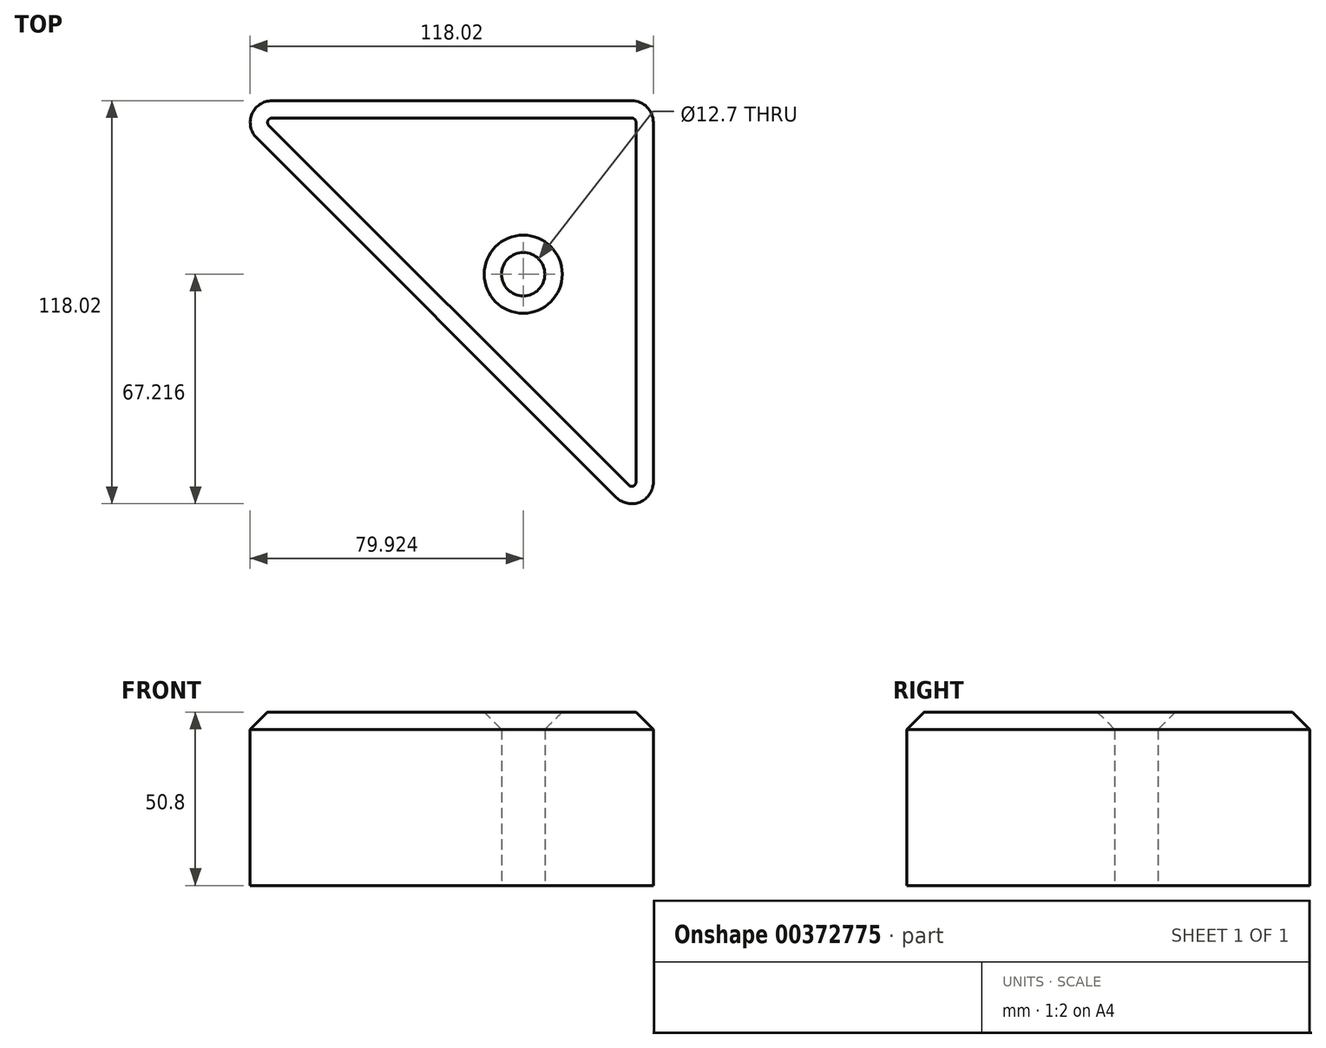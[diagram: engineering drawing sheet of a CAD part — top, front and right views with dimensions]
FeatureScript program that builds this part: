
annotation { "Feature Type Name" : "Feature", "Feature Type Description" : "" }
export const myFeature = defineFeature(function(context is Context, id is Id, definition is map)
    precondition{}
    {
        {
            var Q0;
            Q0=qCreatedBy(makeId("Top.planeOp"),FACE);
            var sketch = newSketch(context, id + "F0", { "sketchPlane" : qUnion([Q0])});
            skLineSegment(sketch, "E0", {"start": v(-67.08, 34.78) * mm, "end": v(38.24, 34.78) * mm});
            skLineSegment(sketch, "E1", {"start": v(44.6, 28.43) * mm, "end": v(44.6, -76.9) * mm});
            skLineSegment(sketch, "E2", {"start": v(33.75, -81.38) * mm, "end": v(-71.57, 23.94) * mm});
            skCircle(sketch, "E3", {"center": v(6.5, -16.02) * mm, "radius": 6.35 * mm});
            skPoint(sketch, "E4.visualSharp", {"position": v(-82.4, 34.78) * mm});
            skArc(sketch, "E4.filletArc", {"start": v(-67.08, 34.78) * mm, "mid": v(-72.94, 30.86) * mm, "end": v(-71.57, 23.94) * mm});
            skPoint(sketch, "E5.visualSharp", {"position": v(44.6, 34.78) * mm});
            skArc(sketch, "E5.filletArc", {"start": v(44.6, 28.43) * mm, "mid": v(42.73, 32.92) * mm, "end": v(38.24, 34.78) * mm});
            skPoint(sketch, "E6.visualSharp", {"position": v(44.6, -92.22) * mm});
            skArc(sketch, "E6.filletArc", {"start": v(33.75, -81.38) * mm, "mid": v(40.67, -82.76) * mm, "end": v(44.6, -76.9) * mm});
            skLineSegment(sketch, "E7", {"start": v(0, 0) * mm, "end": v(6.5, -16.02) * mm, "construction": true});
            skLineSegment(sketch, "E8", {"start": v(6.5, -16.02) * mm, "end": v(0, -16.02) * mm});
            skLineSegment(sketch, "E9", {"start": v(0, -16.02) * mm, "end": v(0, 0) * mm, "construction": true});
            skSolve(sketch);
        }
        {
            var Q0;
            Q0=makeQuery(id+"F0.imprint","IMPRINT",FACE,{"disambiguationData":[TD([[makeQuery(id+"F0.imprint","IMPRINT",EDGE,{"derivedFrom":sQuery(id+"F0.wireOp",EDGE,"E0")}),-1.0]])]});
            extrude(context, id + "F1", {"entities" : qUnion([Q0]), "depth" : 50.8 * mm});
        }
        {
            var Q0;
            Q0=makeQuery(id+"F1.opExtrude","CAP_EDGE",EDGE,{"disambiguationData":[OSD([sQuery(id+"F0.wireOp",EDGE,"E1")])],"isStart":false});
            var Q1;
            Q1=makeQuery(id+"F1.opExtrude","CAP_EDGE",EDGE,{"disambiguationData":[OSD([sQuery(id+"F0.wireOp",EDGE,"E3")])],"isStart":false});
            chamfer(context, id + "F2", {"entities" : qUnion([Q0, Q1]), "width" : 5.08 * mm, "tangentPropagation" : true});
        }
    });
